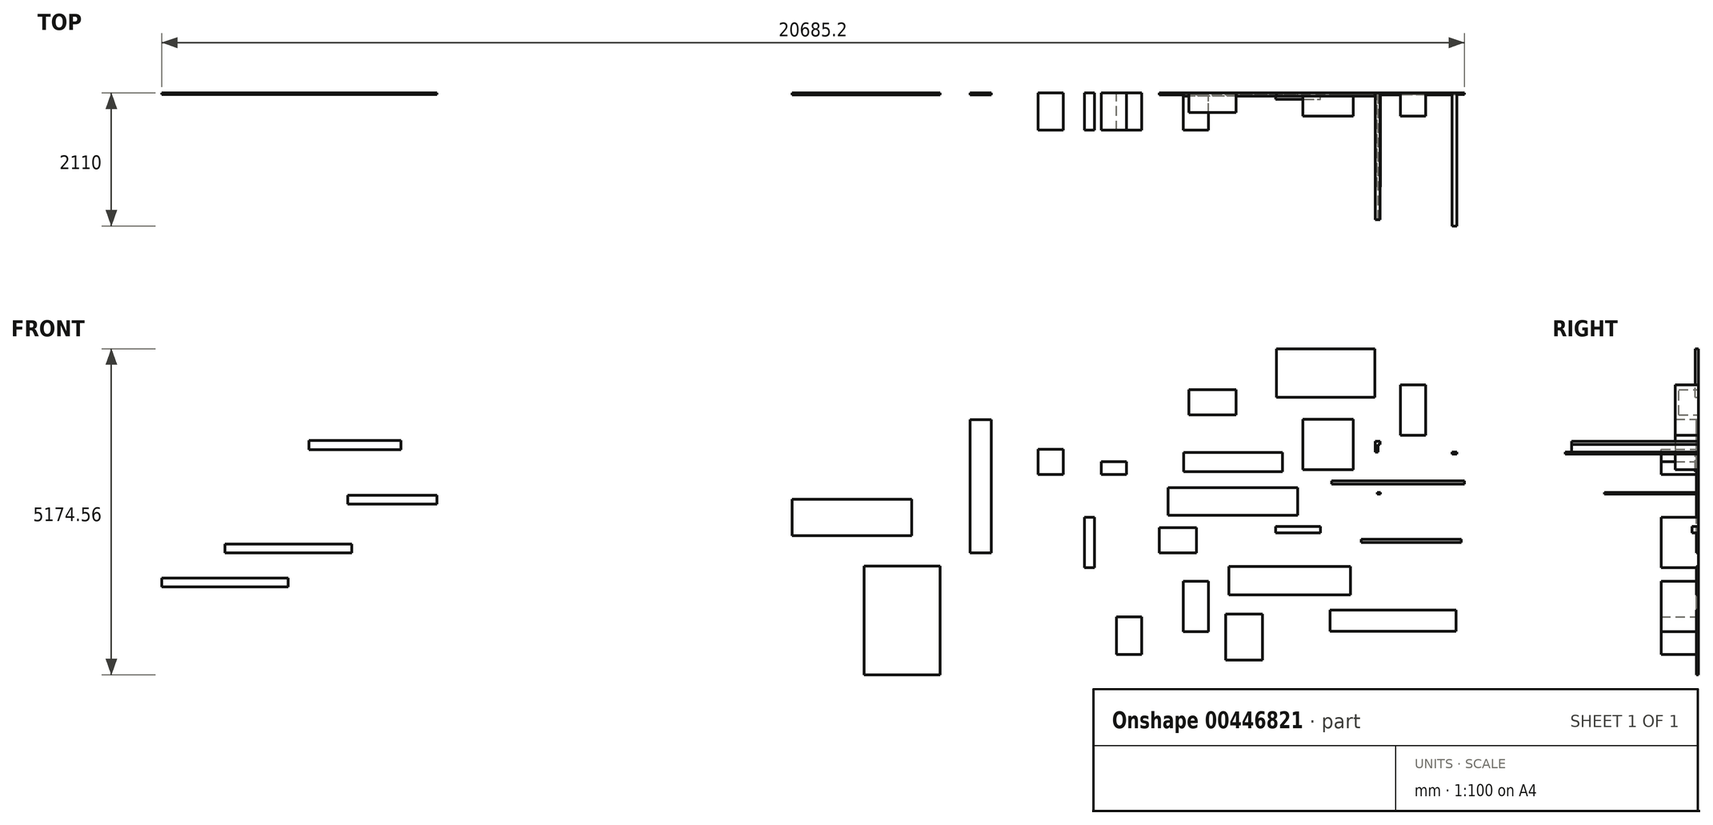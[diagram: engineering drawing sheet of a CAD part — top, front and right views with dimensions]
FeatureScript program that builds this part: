
annotation { "Feature Type Name" : "Feature", "Feature Type Description" : "" }
export const myFeature = defineFeature(function(context is Context, id is Id, definition is map)
    precondition{}
    {
        {
            var Q0;
            Q0=qCreatedBy(makeId("Front.planeOp"),FACE);
            var sketch = newSketch(context, id + "F0", { "sketchPlane" : qUnion([Q0])});
            skLineSegment(sketch, "E0.bottom", {"start": v(-70.34, 315.88) * mm, "end": v(639.66, 315.88) * mm});
            skLineSegment(sketch, "E0.top", {"start": v(-70.34, 415.88) * mm, "end": v(639.66, 415.88) * mm});
            skLineSegment(sketch, "E0.left", {"start": v(-70.34, 315.88) * mm, "end": v(-70.34, 415.88) * mm});
            skLineSegment(sketch, "E0.right", {"start": v(639.66, 315.88) * mm, "end": v(639.66, 415.88) * mm});
            skSolve(sketch);
        }
        {
            var Q0;
            Q0=qSketchRegion(id+"F0",true);
            extrude(context, id + "F1", {"entities" : qUnion([Q0]), "depth" : 100 * mm});
        }
        {
            var Q0;
            Q0=qCreatedBy(makeId("Front.planeOp"),FACE);
            var sketch = newSketch(context, id + "F2", { "sketchPlane" : qUnion([Q0])});
            skLineSegment(sketch, "E1.bottom", {"start": v(2792.12, -1245.36) * mm, "end": v(792.12, -1245.36) * mm});
            skLineSegment(sketch, "E1.top", {"start": v(2792.12, -911.36) * mm, "end": v(792.12, -911.36) * mm});
            skLineSegment(sketch, "E1.left", {"start": v(2792.12, -1245.36) * mm, "end": v(2792.12, -911.36) * mm});
            skLineSegment(sketch, "E1.right", {"start": v(792.12, -1245.36) * mm, "end": v(792.12, -911.36) * mm});
            skPoint(sketch, "E1.middle", {"position": v(1792.12, -1078.36) * mm});
            skSolve(sketch);
        }
        {
            var Q0;
            Q0=qSketchRegion(id+"F2",true);
            extrude(context, id + "F3", {"entities" : qUnion([Q0]), "depth" : 27 * mm});
        }
        {
            var Q0;
            Q0=qCreatedBy(makeId("Front.planeOp"),FACE);
            var sketch = newSketch(context, id + "F4", { "sketchPlane" : qUnion([Q0])});
            skLineSegment(sketch, "E2.bottom", {"start": v(1507.35, 2468.2) * mm, "end": v(-57.65, 2468.2) * mm});
            skLineSegment(sketch, "E2.top", {"start": v(1507.35, 3238.2) * mm, "end": v(-57.65, 3238.2) * mm});
            skLineSegment(sketch, "E2.left", {"start": v(1507.35, 2468.2) * mm, "end": v(1507.35, 3238.2) * mm});
            skLineSegment(sketch, "E2.right", {"start": v(-57.65, 2468.2) * mm, "end": v(-57.65, 3238.2) * mm});
            skPoint(sketch, "E2.middle", {"position": v(724.85, 2853.2) * mm});
            skLineSegment(sketch, "E3.bottom", {"start": v(36.65, 1290.1) * mm, "end": v(-1528.35, 1290.1) * mm});
            skLineSegment(sketch, "E3.top", {"start": v(36.65, 1590.1) * mm, "end": v(-1528.35, 1590.1) * mm});
            skLineSegment(sketch, "E3.left", {"start": v(36.65, 1290.1) * mm, "end": v(36.65, 1590.1) * mm});
            skLineSegment(sketch, "E3.right", {"start": v(-1528.35, 1290.1) * mm, "end": v(-1528.35, 1590.1) * mm});
            skPoint(sketch, "E3.middle", {"position": v(-745.85, 1440.1) * mm});
            skSolve(sketch);
        }
        {
            var Q0;
            Q0=qSketchRegion(id+"F4",true);
            extrude(context, id + "F5", {"entities" : qUnion([Q0]), "depth" : 50 * mm});
        }
        {
            var Q0;
            Q0=qCreatedBy(makeId("Front.planeOp"),FACE);
            var sketch = newSketch(context, id + "F6", { "sketchPlane" : qUnion([Q0])});
            skLineSegment(sketch, "E4", {"start": v(1558.46, 1595.78) * mm, "end": v(1513.46, 1595.78) * mm});
            skLineSegment(sketch, "E5", {"start": v(1513.46, 1595.78) * mm, "end": v(1513.46, 1770.78) * mm});
            skLineSegment(sketch, "E6", {"start": v(1513.46, 1770.78) * mm, "end": v(1588.46, 1770.78) * mm});
            skLineSegment(sketch, "E7", {"start": v(1588.46, 1770.78) * mm, "end": v(1588.46, 1720.78) * mm});
            skLineSegment(sketch, "E8", {"start": v(1588.46, 1720.78) * mm, "end": v(1558.46, 1720.78) * mm});
            skLineSegment(sketch, "E9", {"start": v(1558.46, 1720.78) * mm, "end": v(1558.46, 1595.78) * mm});
            skSolve(sketch);
        }
        {
            var Q0;
            Q0=qSketchRegion(id+"F6",true);
            extrude(context, id + "F7", {"entities" : qUnion([Q0]), "depth" : 2010 * mm});
        }
        {
            var Q0;
            Q0=qCreatedBy(makeId("Front.planeOp"),FACE);
            var sketch = newSketch(context, id + "F8", { "sketchPlane" : qUnion([Q0])});
            skLineSegment(sketch, "E10.bottom", {"start": v(2929.7, 1090.93) * mm, "end": v(819.7, 1090.93) * mm});
            skLineSegment(sketch, "E10.top", {"start": v(2929.7, 1138.93) * mm, "end": v(819.7, 1138.93) * mm});
            skLineSegment(sketch, "E10.left", {"start": v(2929.7, 1090.93) * mm, "end": v(2929.7, 1138.93) * mm});
            skLineSegment(sketch, "E10.right", {"start": v(819.7, 1090.93) * mm, "end": v(819.7, 1138.93) * mm});
            skPoint(sketch, "E10.middle", {"position": v(1874.7, 1114.93) * mm});
            skSolve(sketch);
        }
        {
            var Q0;
            Q0=qSketchRegion(id+"F8",true);
            extrude(context, id + "F9", {"entities" : qUnion([Q0]), "depth" : 24 * mm});
        }
        {
            var Q0;
            Q0=qCreatedBy(makeId("Front.planeOp"),FACE);
            var sketch = newSketch(context, id + "F10", { "sketchPlane" : qUnion([Q0])});
            skLineSegment(sketch, "E11.bottom", {"start": v(2877, 163.53) * mm, "end": v(1288, 163.53) * mm});
            skLineSegment(sketch, "E11.top", {"start": v(2877, 211.53) * mm, "end": v(1288, 211.53) * mm});
            skLineSegment(sketch, "E11.left", {"start": v(2877, 163.53) * mm, "end": v(2877, 211.53) * mm});
            skLineSegment(sketch, "E11.right", {"start": v(1288, 163.53) * mm, "end": v(1288, 211.53) * mm});
            skPoint(sketch, "E11.middle", {"position": v(2082.5, 187.53) * mm});
            skSolve(sketch);
        }
        {
            var Q0;
            Q0=qSketchRegion(id+"F10",true);
            extrude(context, id + "F11", {"entities" : qUnion([Q0]), "depth" : 24 * mm});
        }
        {
            var Q0;
            Q0=qCreatedBy(makeId("Front.planeOp"),FACE);
            var sketch = newSketch(context, id + "F12", { "sketchPlane" : qUnion([Q0])});
            skLineSegment(sketch, "E12.bottom", {"start": v(-5848.88, 271.4) * mm, "end": v(-7747.88, 271.4) * mm});
            skLineSegment(sketch, "E12.top", {"start": v(-5848.88, 851.4) * mm, "end": v(-7747.88, 851.4) * mm});
            skLineSegment(sketch, "E12.left", {"start": v(-5848.88, 271.4) * mm, "end": v(-5848.88, 851.4) * mm});
            skLineSegment(sketch, "E12.right", {"start": v(-7747.88, 271.4) * mm, "end": v(-7747.88, 851.4) * mm});
            skPoint(sketch, "E12.middle", {"position": v(-6798.38, 561.4) * mm});
            skLineSegment(sketch, "E13.bottom", {"start": v(-4585.05, 0) * mm, "end": v(-4919.05, 0) * mm});
            skLineSegment(sketch, "E13.top", {"start": v(-4585.05, 2110) * mm, "end": v(-4919.05, 2110) * mm});
            skLineSegment(sketch, "E13.left", {"start": v(-4585.05, 0) * mm, "end": v(-4585.05, 2110) * mm});
            skLineSegment(sketch, "E13.right", {"start": v(-4919.05, 0) * mm, "end": v(-4919.05, 2110) * mm});
            skPoint(sketch, "E13.middle", {"position": v(-4752.05, 1055) * mm});
            skLineSegment(sketch, "E14.bottom", {"start": v(-5395.23, -1936.35) * mm, "end": v(-6605.51, -1936.35) * mm});
            skLineSegment(sketch, "E14.top", {"start": v(-5395.23, -210.2) * mm, "end": v(-6605.51, -210.2) * mm});
            skLineSegment(sketch, "E14.left", {"start": v(-5395.23, -1936.35) * mm, "end": v(-5395.23, -210.2) * mm});
            skLineSegment(sketch, "E14.right", {"start": v(-6605.51, -1936.35) * mm, "end": v(-6605.51, -210.2) * mm});
            skPoint(sketch, "E14.middle", {"position": v(-6000.37, -1073.28) * mm});
            skSolve(sketch);
        }
        {
            var Q0;
            Q0=qSketchRegion(id+"F12",true);
            extrude(context, id + "F13", {"entities" : qUnion([Q0]), "depth" : 28 * mm});
        }
        {
            var Q0;
            Q0=qCreatedBy(makeId("Front.planeOp"),FACE);
            var sketch = newSketch(context, id + "F14", { "sketchPlane" : qUnion([Q0])});
            skLineSegment(sketch, "E15.bottom", {"start": v(362.1, 2119.75) * mm, "end": v(1162.1, 2119.75) * mm});
            skLineSegment(sketch, "E15.top", {"start": v(362.1, 1319.75) * mm, "end": v(1162.1, 1319.75) * mm});
            skLineSegment(sketch, "E15.left", {"start": v(362.1, 2119.75) * mm, "end": v(362.1, 1319.75) * mm});
            skLineSegment(sketch, "E15.right", {"start": v(1162.1, 2119.75) * mm, "end": v(1162.1, 1319.75) * mm});
            skSolve(sketch);
        }
        {
            var Q0;
            Q0=qSketchRegion(id+"F14",true);
            extrude(context, id + "F15", {"entities" : qUnion([Q0]), "depth" : 366 * mm});
        }
        {
            var Q0;
            Q0=qCreatedBy(makeId("Front.planeOp"),FACE);
            var sketch = newSketch(context, id + "F16", { "sketchPlane" : qUnion([Q0])});
            skLineSegment(sketch, "E16.bottom", {"start": v(1909.96, 1864.78) * mm, "end": v(2309.96, 1864.78) * mm});
            skLineSegment(sketch, "E16.top", {"start": v(1909.96, 2664.78) * mm, "end": v(2309.96, 2664.78) * mm});
            skLineSegment(sketch, "E16.left", {"start": v(1909.96, 1864.78) * mm, "end": v(1909.96, 2664.78) * mm});
            skLineSegment(sketch, "E16.right", {"start": v(2309.96, 1864.78) * mm, "end": v(2309.96, 2664.78) * mm});
            skSolve(sketch);
        }
        {
            var Q0;
            Q0=qSketchRegion(id+"F16",true);
            extrude(context, id + "F17", {"entities" : qUnion([Q0]), "depth" : 366 * mm});
        }
        {
            var Q0;
            Q0=qCreatedBy(makeId("Front.planeOp"),FACE);
            var sketch = newSketch(context, id + "F18", { "sketchPlane" : qUnion([Q0])});
            skLineSegment(sketch, "E17.bottom", {"start": v(-1445.88, 2189.41) * mm, "end": v(-695.88, 2189.41) * mm});
            skLineSegment(sketch, "E17.top", {"start": v(-1445.88, 2589.41) * mm, "end": v(-695.88, 2589.41) * mm});
            skLineSegment(sketch, "E17.left", {"start": v(-1445.88, 2189.41) * mm, "end": v(-1445.88, 2589.41) * mm});
            skLineSegment(sketch, "E17.right", {"start": v(-695.88, 2189.41) * mm, "end": v(-695.88, 2589.41) * mm});
            skSolve(sketch);
        }
        {
            var Q0;
            Q0=qSketchRegion(id+"F18",true);
            extrude(context, id + "F19", {"entities" : qUnion([Q0]), "depth" : 310 * mm});
        }
        {
            var Q0;
            Q0=qCreatedBy(makeId("Front.planeOp"),FACE);
            var sketch = newSketch(context, id + "F20", { "sketchPlane" : qUnion([Q0])});
            skLineSegment(sketch, "E18.bottom", {"start": v(2733.76, 1567.97) * mm, "end": v(2808.76, 1567.97) * mm});
            skLineSegment(sketch, "E18.top", {"start": v(2733.76, 1597.97) * mm, "end": v(2808.76, 1597.97) * mm});
            skLineSegment(sketch, "E18.left", {"start": v(2733.76, 1567.97) * mm, "end": v(2733.76, 1597.97) * mm});
            skLineSegment(sketch, "E18.right", {"start": v(2808.76, 1567.97) * mm, "end": v(2808.76, 1597.97) * mm});
            skSolve(sketch);
        }
        {
            var Q0;
            Q0=qSketchRegion(id+"F20",true);
            extrude(context, id + "F21", {"entities" : qUnion([Q0]), "depth" : 2110 * mm});
        }
        {
            var Q0;
            Q0=qCreatedBy(makeId("Front.planeOp"),FACE);
            var sketch = newSketch(context, id + "F22", { "sketchPlane" : qUnion([Q0])});
            skLineSegment(sketch, "E19.bottom", {"start": v(-2838.93, 1443.37) * mm, "end": v(-2438.93, 1443.37) * mm});
            skLineSegment(sketch, "E19.top", {"start": v(-2838.93, 1243.37) * mm, "end": v(-2438.93, 1243.37) * mm});
            skLineSegment(sketch, "E19.left", {"start": v(-2838.93, 1443.37) * mm, "end": v(-2838.93, 1243.37) * mm});
            skLineSegment(sketch, "E19.right", {"start": v(-2438.93, 1443.37) * mm, "end": v(-2438.93, 1243.37) * mm});
            skLineSegment(sketch, "E20.bottom", {"start": v(-3438.78, 1242.1) * mm, "end": v(-3838.78, 1242.1) * mm});
            skLineSegment(sketch, "E20.top", {"start": v(-3438.78, 1642.1) * mm, "end": v(-3838.78, 1642.1) * mm});
            skLineSegment(sketch, "E20.left", {"start": v(-3438.78, 1242.1) * mm, "end": v(-3438.78, 1642.1) * mm});
            skLineSegment(sketch, "E20.right", {"start": v(-3838.78, 1242.1) * mm, "end": v(-3838.78, 1642.1) * mm});
            skSolve(sketch);
        }
        {
            var Q0;
            Q0=qSketchRegion(id+"F22",true);
            extrude(context, id + "F23", {"entities" : qUnion([Q0]), "depth" : 590 * mm});
        }
        {
            var Q0;
            Q0=qCreatedBy(makeId("Front.planeOp"),FACE);
            var sketch = newSketch(context, id + "F24", { "sketchPlane" : qUnion([Q0])});
            skLineSegment(sketch, "E21.bottom", {"start": v(-2596.9, -1617.65) * mm, "end": v(-2196.9, -1617.65) * mm});
            skLineSegment(sketch, "E21.top", {"start": v(-2596.9, -1017.65) * mm, "end": v(-2196.9, -1017.65) * mm});
            skLineSegment(sketch, "E21.left", {"start": v(-2596.9, -1617.65) * mm, "end": v(-2596.9, -1017.65) * mm});
            skLineSegment(sketch, "E21.right", {"start": v(-2196.9, -1617.65) * mm, "end": v(-2196.9, -1017.65) * mm});
            skSolve(sketch);
        }
        {
            var Q0;
            Q0=qSketchRegion(id+"F24",true);
            extrude(context, id + "F25", {"entities" : qUnion([Q0]), "depth" : 590 * mm});
        }
        {
            var Q0;
            Q0=qCreatedBy(makeId("Front.planeOp"),FACE);
            var sketch = newSketch(context, id + "F26", { "sketchPlane" : qUnion([Q0])});
            skLineSegment(sketch, "E22.bottom", {"start": v(-1324.59, 0) * mm, "end": v(-1914.59, 0) * mm});
            skLineSegment(sketch, "E22.top", {"start": v(-1324.59, 400) * mm, "end": v(-1914.59, 400) * mm});
            skLineSegment(sketch, "E22.left", {"start": v(-1324.59, 0) * mm, "end": v(-1324.59, 400) * mm});
            skLineSegment(sketch, "E22.right", {"start": v(-1914.59, 0) * mm, "end": v(-1914.59, 400) * mm});
            skSolve(sketch);
        }
        {
            var Q0;
            Q0=qSketchRegion(id+"F26",true);
            extrude(context, id + "F27", {"entities" : qUnion([Q0]), "depth" : 28 * mm});
        }
        {
            var Q0;
            Q0=qCreatedBy(makeId("Front.planeOp"),FACE);
            var sketch = newSketch(context, id + "F28", { "sketchPlane" : qUnion([Q0])});
            skLineSegment(sketch, "E23.bottom", {"start": v(-3107.87, -233.81) * mm, "end": v(-2947.87, -233.81) * mm});
            skLineSegment(sketch, "E23.top", {"start": v(-3107.87, 566.19) * mm, "end": v(-2947.87, 566.19) * mm});
            skLineSegment(sketch, "E23.left", {"start": v(-3107.87, -233.81) * mm, "end": v(-3107.87, 566.19) * mm});
            skLineSegment(sketch, "E23.right", {"start": v(-2947.87, -233.81) * mm, "end": v(-2947.87, 566.19) * mm});
            skSolve(sketch);
        }
        {
            var Q0;
            Q0=qSketchRegion(id+"F28",true);
            extrude(context, id + "F29", {"entities" : qUnion([Q0]), "depth" : 590 * mm});
        }
        {
            var Q0;
            Q0=qCreatedBy(makeId("Front.planeOp"),FACE);
            var sketch = newSketch(context, id + "F30", { "sketchPlane" : qUnion([Q0])});
            skLineSegment(sketch, "E24.bottom", {"start": v(-1534.1, -1253.8) * mm, "end": v(-1134.1, -1253.8) * mm});
            skLineSegment(sketch, "E24.top", {"start": v(-1534.1, -453.8) * mm, "end": v(-1134.1, -453.8) * mm});
            skLineSegment(sketch, "E24.left", {"start": v(-1534.1, -1253.8) * mm, "end": v(-1534.1, -453.8) * mm});
            skLineSegment(sketch, "E24.right", {"start": v(-1134.1, -1253.8) * mm, "end": v(-1134.1, -453.8) * mm});
            skSolve(sketch);
        }
        {
            var Q0;
            Q0=qSketchRegion(id+"F30",true);
            extrude(context, id + "F31", {"entities" : qUnion([Q0]), "depth" : 590 * mm});
        }
        {
            var Q0;
            Q0=qCreatedBy(makeId("Front.planeOp"),FACE);
            var sketch = newSketch(context, id + "F32", { "sketchPlane" : qUnion([Q0])});
            skLineSegment(sketch, "E25.bottom", {"start": v(-1778.46, 1035.73) * mm, "end": v(281.54, 1035.73) * mm});
            skLineSegment(sketch, "E25.top", {"start": v(-1778.46, 594.73) * mm, "end": v(281.54, 594.73) * mm});
            skLineSegment(sketch, "E25.left", {"start": v(-1778.46, 1035.73) * mm, "end": v(-1778.46, 594.73) * mm});
            skLineSegment(sketch, "E25.right", {"start": v(281.54, 1035.73) * mm, "end": v(281.54, 594.73) * mm});
            skLineSegment(sketch, "E26.bottom", {"start": v(-815.1, -217.6) * mm, "end": v(1115.9, -217.6) * mm});
            skLineSegment(sketch, "E26.top", {"start": v(-815.1, -667.6) * mm, "end": v(1115.9, -667.6) * mm});
            skLineSegment(sketch, "E26.left", {"start": v(-815.1, -217.6) * mm, "end": v(-815.1, -667.6) * mm});
            skLineSegment(sketch, "E26.right", {"start": v(1115.9, -217.6) * mm, "end": v(1115.9, -667.6) * mm});
            skLineSegment(sketch, "E27.bottom", {"start": v(-866.07, -974.82) * mm, "end": v(-276.07, -974.82) * mm});
            skLineSegment(sketch, "E27.top", {"start": v(-866.07, -1705.82) * mm, "end": v(-276.07, -1705.82) * mm});
            skLineSegment(sketch, "E27.left", {"start": v(-866.07, -974.82) * mm, "end": v(-866.07, -1705.82) * mm});
            skLineSegment(sketch, "E27.right", {"start": v(-276.07, -974.82) * mm, "end": v(-276.07, -1705.82) * mm});
            skSolve(sketch);
        }
        {
            var Q0;
            Q0=qSketchRegion(id+"F32",true);
            extrude(context, id + "F33", {"entities" : qUnion([Q0]), "depth" : 27 * mm});
        }
        {
            var Q0;
            Q0=qCreatedBy(makeId("Front.planeOp"),FACE);
            var sketch = newSketch(context, id + "F34", { "sketchPlane" : qUnion([Q0])});
            skLineSegment(sketch, "E28.bottom", {"start": v(1541.46, 958.6) * mm, "end": v(1591.46, 958.6) * mm});
            skLineSegment(sketch, "E28.top", {"start": v(1541.46, 928.6) * mm, "end": v(1591.46, 928.6) * mm});
            skLineSegment(sketch, "E28.left", {"start": v(1541.46, 958.6) * mm, "end": v(1541.46, 928.6) * mm});
            skLineSegment(sketch, "E28.right", {"start": v(1591.46, 958.6) * mm, "end": v(1591.46, 928.6) * mm});
            skSolve(sketch);
        }
        {
            var Q0;
            Q0=qSketchRegion(id+"F34",true);
            extrude(context, id + "F35", {"entities" : qUnion([Q0]), "depth" : 1490 * mm});
        }
        {
            var Q0;
            Q0=qCreatedBy(makeId("Front.planeOp"),FACE);
            var sketch = newSketch(context, id + "F36", { "sketchPlane" : qUnion([Q0])});
            skLineSegment(sketch, "E29.bottom", {"start": v(-13386.96, 771.48) * mm, "end": v(-14801.96, 771.48) * mm});
            skLineSegment(sketch, "E29.top", {"start": v(-13386.96, 911.48) * mm, "end": v(-14801.96, 911.48) * mm});
            skLineSegment(sketch, "E29.left", {"start": v(-13386.96, 771.48) * mm, "end": v(-13386.96, 911.48) * mm});
            skLineSegment(sketch, "E29.right", {"start": v(-14801.96, 771.48) * mm, "end": v(-14801.96, 911.48) * mm});
            skPoint(sketch, "E29.middle", {"position": v(-14094.46, 841.48) * mm});
            skLineSegment(sketch, "E30.bottom", {"start": v(-14740.52, 0) * mm, "end": v(-16750.52, 0) * mm});
            skLineSegment(sketch, "E30.top", {"start": v(-14740.52, 140) * mm, "end": v(-16750.52, 140) * mm});
            skLineSegment(sketch, "E30.left", {"start": v(-14740.52, 0) * mm, "end": v(-14740.52, 140) * mm});
            skLineSegment(sketch, "E30.right", {"start": v(-16750.52, 0) * mm, "end": v(-16750.52, 140) * mm});
            skPoint(sketch, "E30.middle", {"position": v(-15745.52, 70) * mm});
            skLineSegment(sketch, "E31.bottom", {"start": v(-13955.79, 1639.47) * mm, "end": v(-15416.79, 1639.47) * mm});
            skLineSegment(sketch, "E31.top", {"start": v(-13955.79, 1779.47) * mm, "end": v(-15416.79, 1779.47) * mm});
            skLineSegment(sketch, "E31.left", {"start": v(-13955.79, 1639.47) * mm, "end": v(-13955.79, 1779.47) * mm});
            skLineSegment(sketch, "E31.right", {"start": v(-15416.79, 1639.47) * mm, "end": v(-15416.79, 1779.47) * mm});
            skPoint(sketch, "E31.middle", {"position": v(-14686.29, 1709.47) * mm});
            skLineSegment(sketch, "E32.bottom", {"start": v(-15745.52, -542.55) * mm, "end": v(-17755.52, -542.55) * mm});
            skLineSegment(sketch, "E32.top", {"start": v(-15745.52, -402.55) * mm, "end": v(-17755.52, -402.55) * mm});
            skLineSegment(sketch, "E32.left", {"start": v(-15745.52, -542.55) * mm, "end": v(-15745.52, -402.55) * mm});
            skLineSegment(sketch, "E32.right", {"start": v(-17755.52, -542.55) * mm, "end": v(-17755.52, -402.55) * mm});
            skPoint(sketch, "E32.middle", {"position": v(-16750.52, -472.55) * mm});
            skSolve(sketch);
        }
        {
            var Q0;
            Q0 = qSketchRegion(id + "F36", true);
            extrude(context, id + "F37", {"entities" : qUnion([Q0]), "depth" : 23 * mm});
        }
    });
